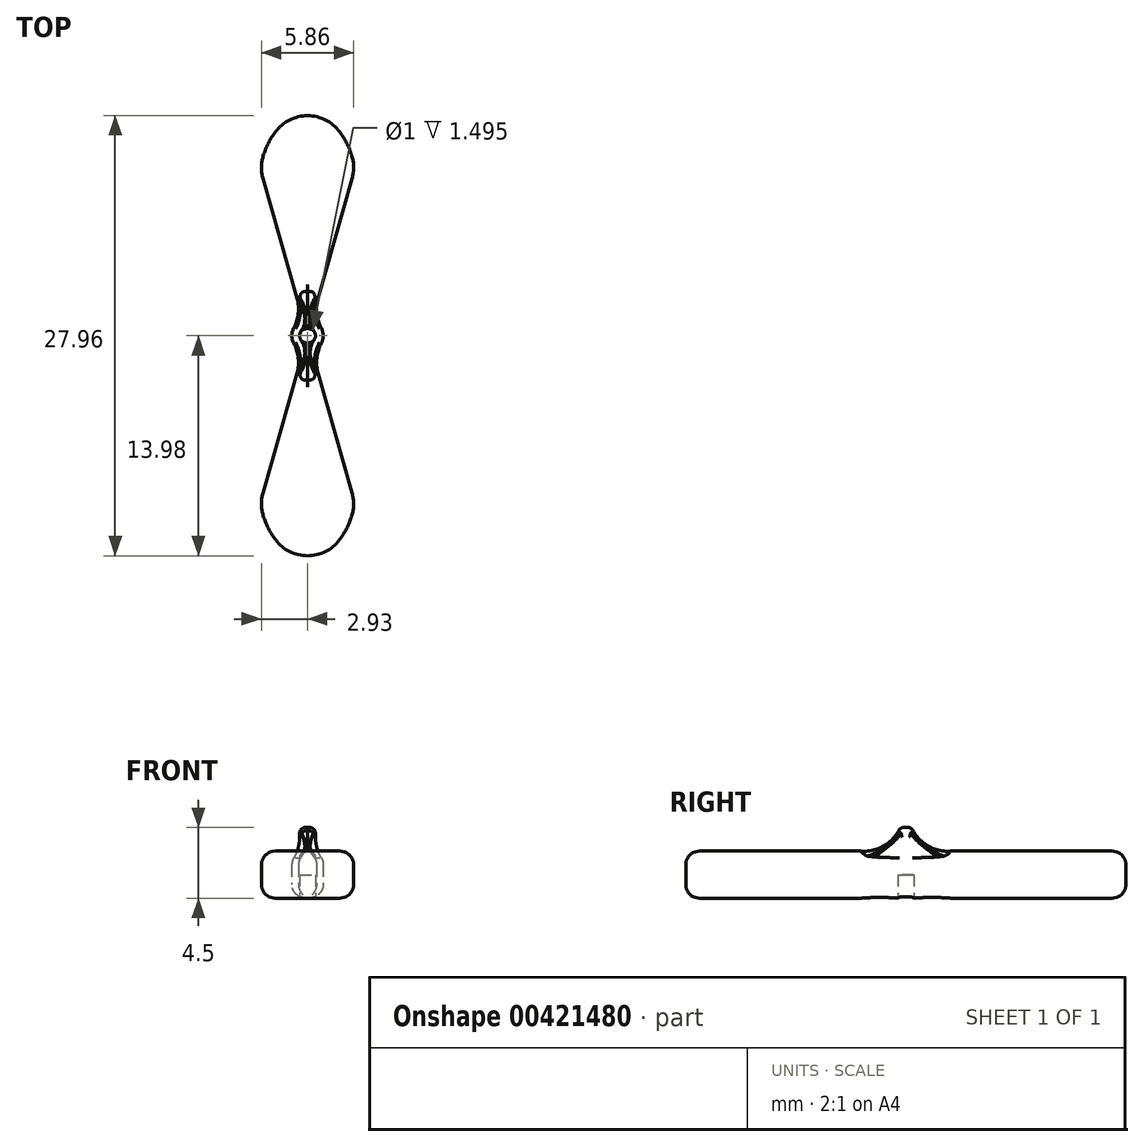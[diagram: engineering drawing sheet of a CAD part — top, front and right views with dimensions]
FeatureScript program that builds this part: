
annotation { "Feature Type Name" : "Feature", "Feature Type Description" : "" }
export const myFeature = defineFeature(function(context is Context, id is Id, definition is map)
    precondition{}
    {
        {
            var Q0;
            Q0=qCreatedBy(makeId("Top.planeOp"),FACE);
            var sketch = newSketch(context, id + "F0", { "sketchPlane" : qUnion([Q0])});
            skLineSegment(sketch, "E0", {"start": v(0, 0) * mm, "end": v(0, 15) * mm});
            skLineSegment(sketch, "E1", {"start": v(0, 15) * mm, "end": v(3, 15) * mm});
            skLineSegment(sketch, "E2", {"start": v(3, 15) * mm, "end": v(3, 10.58) * mm});
            skLineSegment(sketch, "E3", {"start": v(3, 10.58) * mm, "end": v(0, 0) * mm});
            skLineSegment(sketch, "E4.MirrorCS", {"start": v(0, 15) * mm, "end": v(-3, 15) * mm});
            skLineSegment(sketch, "E5.MirrorCS", {"start": v(-3, 15) * mm, "end": v(-3, 10.58) * mm});
            skLineSegment(sketch, "E6.MirrorCS", {"start": v(-3, 10.58) * mm, "end": v(0, 0) * mm});
            skLineSegment(sketch, "E7.MirrorCS", {"start": v(3, -10.58) * mm, "end": v(0, 0) * mm});
            skLineSegment(sketch, "E8.MirrorCS", {"start": v(-3, -10.58) * mm, "end": v(0, 0) * mm});
            skLineSegment(sketch, "E9.MirrorCS", {"start": v(3, -15) * mm, "end": v(3, -10.58) * mm});
            skLineSegment(sketch, "E10.MirrorCS", {"start": v(0, -15) * mm, "end": v(-3, -15) * mm});
            skLineSegment(sketch, "E11.MirrorCS", {"start": v(-3, -15) * mm, "end": v(-3, -10.58) * mm});
            skLineSegment(sketch, "E12.MirrorCS", {"start": v(0, -15) * mm, "end": v(3, -15) * mm});
            skLineSegment(sketch, "E13.MirrorCS", {"start": v(0, 0) * mm, "end": v(0, -15) * mm});
            skCircle(sketch, "E14", {"center": v(0, 0) * mm, "radius": 1 * mm});
            skSolve(sketch);
        }
        {
            var Q0;
            Q0 = qSketchRegion(id + "F0", true);
            extrude(context, id + "F1", {"entities" : qUnion([Q0]), "depth" : 3 * mm});
        }
        {
            var Q0;
            Q0=makeQuery(id+"F1.opExtrude","SWEPT_EDGE",EDGE,{"disambiguationData":[OSD([sQuery(id+"F0.wireOp",EDGE,"E9.MirrorCS"),sQuery(id+"F0.wireOp",EDGE,"E12.MirrorCS")])]});
            var Q1;
            Q1=makeQuery(id+"F1.opExtrude","SWEPT_EDGE",EDGE,{"disambiguationData":[OSD([sQuery(id+"F0.wireOp",EDGE,"E10.MirrorCS"),sQuery(id+"F0.wireOp",EDGE,"E11.MirrorCS")])]});
            var Q2;
            Q2=makeQuery(id+"F1.opExtrude","SWEPT_EDGE",EDGE,{"disambiguationData":[OSD([sQuery(id+"F0.wireOp",EDGE,"E1"),sQuery(id+"F0.wireOp",EDGE,"E2")])]});
            var Q3;
            Q3=makeQuery(id+"F1.opExtrude","SWEPT_EDGE",EDGE,{"disambiguationData":[OSD([sQuery(id+"F0.wireOp",EDGE,"E4.MirrorCS"),sQuery(id+"F0.wireOp",EDGE,"E5.MirrorCS")])]});
            fillet(context, id + "F2", {"entities" : qUnion([Q0, Q1, Q2, Q3]), "radius" : 5.08 * mm, "tangentPropagation" : true, "allowEdgeOverflow" : false});
        }
        {
            var Q0;
            Q0=makeQuery(id+"F2.opFillet","BLEND_EDGE",EDGE,{"blendedFrom":[makeQuery(id+"F1.opExtrude","SWEPT_EDGE",EDGE,{"disambiguationData":[OSD([sQuery(id+"F0.wireOp",EDGE,"E4.MirrorCS"),sQuery(id+"F0.wireOp",EDGE,"E5.MirrorCS")])]}),makeQuery(id+"F1.opExtrude","SWEPT_FACE",FACE,{"disambiguationData":[OSD([sQuery(id+"F0.wireOp",EDGE,"E6.MirrorCS")])]})],"blendedInto":[makeQuery(id+"F1.opExtrude","SWEPT_FACE",FACE,{"disambiguationData":[OSD([sQuery(id+"F0.wireOp",EDGE,"E6.MirrorCS")])]})]});
            var Q1;
            Q1=makeQuery(id+"F2.opFillet","BLEND_EDGE",EDGE,{"blendedFrom":[makeQuery(id+"F1.opExtrude","SWEPT_EDGE",EDGE,{"disambiguationData":[OSD([sQuery(id+"F0.wireOp",EDGE,"E1"),sQuery(id+"F0.wireOp",EDGE,"E2")])]}),makeQuery(id+"F1.opExtrude","SWEPT_FACE",FACE,{"disambiguationData":[OSD([sQuery(id+"F0.wireOp",EDGE,"E3")])]})],"blendedInto":[makeQuery(id+"F1.opExtrude","SWEPT_FACE",FACE,{"disambiguationData":[OSD([sQuery(id+"F0.wireOp",EDGE,"E3")])]})]});
            var Q2;
            Q2=makeQuery(id+"F2.opFillet","BLEND_EDGE",EDGE,{"blendedFrom":[makeQuery(id+"F1.opExtrude","SWEPT_EDGE",EDGE,{"disambiguationData":[OSD([sQuery(id+"F0.wireOp",EDGE,"E9.MirrorCS"),sQuery(id+"F0.wireOp",EDGE,"E12.MirrorCS")])]}),makeQuery(id+"F1.opExtrude","SWEPT_FACE",FACE,{"disambiguationData":[OSD([sQuery(id+"F0.wireOp",EDGE,"E7.MirrorCS")])]})],"blendedInto":[makeQuery(id+"F1.opExtrude","SWEPT_FACE",FACE,{"disambiguationData":[OSD([sQuery(id+"F0.wireOp",EDGE,"E7.MirrorCS")])]})]});
            var Q3;
            Q3=makeQuery(id+"F2.opFillet","BLEND_EDGE",EDGE,{"blendedFrom":[makeQuery(id+"F1.opExtrude","SWEPT_EDGE",EDGE,{"disambiguationData":[OSD([sQuery(id+"F0.wireOp",EDGE,"E10.MirrorCS"),sQuery(id+"F0.wireOp",EDGE,"E11.MirrorCS")])]}),makeQuery(id+"F1.opExtrude","SWEPT_FACE",FACE,{"disambiguationData":[OSD([sQuery(id+"F0.wireOp",EDGE,"E8.MirrorCS")])]})],"blendedInto":[makeQuery(id+"F1.opExtrude","SWEPT_FACE",FACE,{"disambiguationData":[OSD([sQuery(id+"F0.wireOp",EDGE,"E8.MirrorCS")])]})]});
            var Q4;
            Q4=makeQuery(id+"F2.opFillet","BLEND_EDGE",EDGE,{"blendedFrom":[makeQuery(id+"F1.opExtrude","SWEPT_EDGE",EDGE,{"disambiguationData":[OSD([sQuery(id+"F0.wireOp",EDGE,"E9.MirrorCS"),sQuery(id+"F0.wireOp",EDGE,"E12.MirrorCS")])]}),makeQuery(id+"F1.opExtrude","SWEPT_EDGE",EDGE,{"disambiguationData":[OSD([sQuery(id+"F0.wireOp",EDGE,"E10.MirrorCS"),sQuery(id+"F0.wireOp",EDGE,"E11.MirrorCS")])]})],"blendedInto":[]});
            var Q5;
            Q5=makeQuery(id+"F2.opFillet","BLEND_EDGE",EDGE,{"blendedFrom":[makeQuery(id+"F1.opExtrude","SWEPT_EDGE",EDGE,{"disambiguationData":[OSD([sQuery(id+"F0.wireOp",EDGE,"E1"),sQuery(id+"F0.wireOp",EDGE,"E2")])]}),makeQuery(id+"F1.opExtrude","SWEPT_EDGE",EDGE,{"disambiguationData":[OSD([sQuery(id+"F0.wireOp",EDGE,"E4.MirrorCS"),sQuery(id+"F0.wireOp",EDGE,"E5.MirrorCS")])]})],"blendedInto":[]});
            fillet(context, id + "F3", {"entities" : qUnion([Q0, Q1, Q2, Q3, Q4, Q5]), "radius" : 2.54 * mm, "tangentPropagation" : true, "allowEdgeOverflow" : false});
        }
        {
            var Q0;
            Q0 = qSketchRegion(id + "F0", true);
            extrude(context, id + "F4", {"entities" : qUnion([Q0]), "operationType" : NewBodyOperationType.ADD, "depth" : 3 * mm});
        }
        {
            var Q0;
            Q0=makeQuery(id+"F4.opExtrude","SWEPT_EDGE",EDGE,{"disambiguationData":[OSD([sQuery(id+"F0.wireOp",EDGE,"E4.MirrorCS"),sQuery(id+"F0.wireOp",EDGE,"E5.MirrorCS")])]});
            var Q1;
            Q1=makeQuery(id+"F4.opExtrude","SWEPT_EDGE",EDGE,{"disambiguationData":[OSD([sQuery(id+"F0.wireOp",EDGE,"E1"),sQuery(id+"F0.wireOp",EDGE,"E2")])]});
            var Q2;
            Q2=makeQuery(id+"F4.opExtrude","SWEPT_EDGE",EDGE,{"disambiguationData":[OSD([sQuery(id+"F0.wireOp",EDGE,"E10.MirrorCS"),sQuery(id+"F0.wireOp",EDGE,"E11.MirrorCS")])]});
            var Q3;
            Q3=makeQuery(id+"F4.opExtrude","SWEPT_EDGE",EDGE,{"disambiguationData":[OSD([sQuery(id+"F0.wireOp",EDGE,"E9.MirrorCS"),sQuery(id+"F0.wireOp",EDGE,"E12.MirrorCS")])]});
            fillet(context, id + "F5", {"entities" : qUnion([Q0, Q1, Q2, Q3]), "radius" : 5.08 * mm, "tangentPropagation" : true, "allowEdgeOverflow" : false});
        }
        {
            var Q0;
            {var subQ0=sQuery(id+"F0.wireOp",EDGE,"E6.MirrorCS");Q0=makeQuery(id+"F5.opFillet","BLEND_EDGE",EDGE,{"blendedFrom":[makeQuery(id+"F4.opExtrude","SWEPT_EDGE",EDGE,{"disambiguationData":[OSD([sQuery(id+"F0.wireOp",EDGE,"E4.MirrorCS"),sQuery(id+"F0.wireOp",EDGE,"E5.MirrorCS")])]}),makeQuery(id+"F4.boolean.opBoolean","MERGE",FACE,{"derivedFrom":[makeQuery(id+"F1.opExtrude","SWEPT_FACE",FACE,{"disambiguationData":[OSD([subQ0])]}),makeQuery(id+"F4.opExtrude","SWEPT_FACE",FACE,{"disambiguationData":[OSD([subQ0])]})]})],"blendedInto":[makeQuery(id+"F4.boolean.opBoolean","MERGE",FACE,{"derivedFrom":[makeQuery(id+"F1.opExtrude","SWEPT_FACE",FACE,{"disambiguationData":[OSD([subQ0])]}),makeQuery(id+"F4.opExtrude","SWEPT_FACE",FACE,{"disambiguationData":[OSD([subQ0])]})]})]});}
            var Q1;
            Q1=makeQuery(id+"F5.opFillet","BLEND_EDGE",EDGE,{"blendedFrom":[makeQuery(id+"F4.opExtrude","SWEPT_EDGE",EDGE,{"disambiguationData":[OSD([sQuery(id+"F0.wireOp",EDGE,"E1"),sQuery(id+"F0.wireOp",EDGE,"E2")])]}),makeQuery(id+"F4.opExtrude","SWEPT_EDGE",EDGE,{"disambiguationData":[OSD([sQuery(id+"F0.wireOp",EDGE,"E4.MirrorCS"),sQuery(id+"F0.wireOp",EDGE,"E5.MirrorCS")])]})],"blendedInto":[]});
            var Q2;
            {var subQ0=sQuery(id+"F0.wireOp",EDGE,"E3");Q2=makeQuery(id+"F5.opFillet","BLEND_EDGE",EDGE,{"blendedFrom":[makeQuery(id+"F4.opExtrude","SWEPT_EDGE",EDGE,{"disambiguationData":[OSD([sQuery(id+"F0.wireOp",EDGE,"E1"),sQuery(id+"F0.wireOp",EDGE,"E2")])]}),makeQuery(id+"F4.boolean.opBoolean","MERGE",FACE,{"derivedFrom":[makeQuery(id+"F1.opExtrude","SWEPT_FACE",FACE,{"disambiguationData":[OSD([subQ0])]}),makeQuery(id+"F4.opExtrude","SWEPT_FACE",FACE,{"disambiguationData":[OSD([subQ0])]})]})],"blendedInto":[makeQuery(id+"F4.boolean.opBoolean","MERGE",FACE,{"derivedFrom":[makeQuery(id+"F1.opExtrude","SWEPT_FACE",FACE,{"disambiguationData":[OSD([subQ0])]}),makeQuery(id+"F4.opExtrude","SWEPT_FACE",FACE,{"disambiguationData":[OSD([subQ0])]})]})]});}
            var Q3;
            {var subQ0=sQuery(id+"F0.wireOp",EDGE,"E7.MirrorCS");Q3=makeQuery(id+"F5.opFillet","BLEND_EDGE",EDGE,{"blendedFrom":[makeQuery(id+"F4.opExtrude","SWEPT_EDGE",EDGE,{"disambiguationData":[OSD([sQuery(id+"F0.wireOp",EDGE,"E9.MirrorCS"),sQuery(id+"F0.wireOp",EDGE,"E12.MirrorCS")])]}),makeQuery(id+"F4.boolean.opBoolean","MERGE",FACE,{"derivedFrom":[makeQuery(id+"F1.opExtrude","SWEPT_FACE",FACE,{"disambiguationData":[OSD([subQ0])]}),makeQuery(id+"F4.opExtrude","SWEPT_FACE",FACE,{"disambiguationData":[OSD([subQ0])]})]})],"blendedInto":[makeQuery(id+"F4.boolean.opBoolean","MERGE",FACE,{"derivedFrom":[makeQuery(id+"F1.opExtrude","SWEPT_FACE",FACE,{"disambiguationData":[OSD([subQ0])]}),makeQuery(id+"F4.opExtrude","SWEPT_FACE",FACE,{"disambiguationData":[OSD([subQ0])]})]})]});}
            var Q4;
            {var subQ0=sQuery(id+"F0.wireOp",EDGE,"E8.MirrorCS");Q4=makeQuery(id+"F5.opFillet","BLEND_EDGE",EDGE,{"blendedFrom":[makeQuery(id+"F4.opExtrude","SWEPT_EDGE",EDGE,{"disambiguationData":[OSD([sQuery(id+"F0.wireOp",EDGE,"E10.MirrorCS"),sQuery(id+"F0.wireOp",EDGE,"E11.MirrorCS")])]}),makeQuery(id+"F4.boolean.opBoolean","MERGE",FACE,{"derivedFrom":[makeQuery(id+"F1.opExtrude","SWEPT_FACE",FACE,{"disambiguationData":[OSD([subQ0])]}),makeQuery(id+"F4.opExtrude","SWEPT_FACE",FACE,{"disambiguationData":[OSD([subQ0])]})]})],"blendedInto":[makeQuery(id+"F4.boolean.opBoolean","MERGE",FACE,{"derivedFrom":[makeQuery(id+"F1.opExtrude","SWEPT_FACE",FACE,{"disambiguationData":[OSD([subQ0])]}),makeQuery(id+"F4.opExtrude","SWEPT_FACE",FACE,{"disambiguationData":[OSD([subQ0])]})]})]});}
            var Q5;
            Q5=makeQuery(id+"F1.opExtrude","SWEPT_EDGE",EDGE,{"disambiguationData":[OSD([sQuery(id+"F0.wireOp",EDGE,"E8.MirrorCS"),sQuery(id+"F0.wireOp",EDGE,"E14")])]});
            var Q6;
            Q6=makeQuery(id+"F1.opExtrude","SWEPT_EDGE",EDGE,{"disambiguationData":[OSD([sQuery(id+"F0.wireOp",EDGE,"E6.MirrorCS"),sQuery(id+"F0.wireOp",EDGE,"E14")])]});
            var Q7;
            Q7=makeQuery(id+"F1.opExtrude","SWEPT_EDGE",EDGE,{"disambiguationData":[OSD([sQuery(id+"F0.wireOp",EDGE,"E7.MirrorCS"),sQuery(id+"F0.wireOp",EDGE,"E14")])]});
            var Q8;
            Q8=makeQuery(id+"F1.opExtrude","SWEPT_EDGE",EDGE,{"disambiguationData":[OSD([sQuery(id+"F0.wireOp",EDGE,"E3"),sQuery(id+"F0.wireOp",EDGE,"E14")])]});
            var Q9;
            Q9=makeQuery(id+"F5.opFillet","BLEND_EDGE",EDGE,{"blendedFrom":[makeQuery(id+"F4.opExtrude","SWEPT_EDGE",EDGE,{"disambiguationData":[OSD([sQuery(id+"F0.wireOp",EDGE,"E9.MirrorCS"),sQuery(id+"F0.wireOp",EDGE,"E12.MirrorCS")])]}),makeQuery(id+"F4.opExtrude","SWEPT_EDGE",EDGE,{"disambiguationData":[OSD([sQuery(id+"F0.wireOp",EDGE,"E10.MirrorCS"),sQuery(id+"F0.wireOp",EDGE,"E11.MirrorCS")])]})],"blendedInto":[]});
            fillet(context, id + "F6", {"entities" : qUnion([Q0, Q1, Q2, Q3, Q4, Q5, Q6, Q7, Q8, Q9]), "radius" : 2.54 * mm, "tangentPropagation" : true, "allowEdgeOverflow" : false});
        }
        {
            var Q0;
            {var subQ0=sQuery(id+"F0.wireOp",EDGE,"E14");var subQ1=sQuery(id+"F0.wireOp",EDGE,"E12.MirrorCS");var subQ2=sQuery(id+"F0.wireOp",EDGE,"E11.MirrorCS");var subQ3=sQuery(id+"F0.wireOp",EDGE,"E10.MirrorCS");var subQ4=sQuery(id+"F0.wireOp",EDGE,"E9.MirrorCS");var subQ5=sQuery(id+"F0.wireOp",EDGE,"E8.MirrorCS");var subQ6=sQuery(id+"F0.wireOp",EDGE,"E7.MirrorCS");var subQ7=sQuery(id+"F0.wireOp",EDGE,"E6.MirrorCS");var subQ8=sQuery(id+"F0.wireOp",EDGE,"E5.MirrorCS");var subQ9=sQuery(id+"F0.wireOp",EDGE,"E4.MirrorCS");var subQ10=sQuery(id+"F0.wireOp",EDGE,"E3");var subQ11=sQuery(id+"F0.wireOp",EDGE,"E2");var subQ12=sQuery(id+"F0.wireOp",EDGE,"E1");Q0=makeQuery(id+"F4.boolean.opBoolean","MERGE",FACE,{"derivedFrom":[makeQuery(id+"F1.opExtrude","CAP_FACE",FACE,{"disambiguationData":[OSD([subQ12,subQ11,subQ10,subQ9,subQ8,subQ7,subQ6,subQ5,subQ4,subQ3,subQ2,subQ1,subQ0])],"isStart":true}),makeQuery(id+"F4.opExtrude","CAP_FACE",FACE,{"disambiguationData":[OSD([subQ12,subQ11,subQ10,subQ9,subQ8,subQ7,subQ6,subQ5,subQ4,subQ3,subQ2,subQ1,subQ0])],"isStart":true})]});}
            var sketch = newSketch(context, id + "F7", { "sketchPlane" : qUnion([Q0])});
            skCircle(sketch, "E15", {"center": v(0, 0) * mm, "radius": 0.5 * mm});
            skSolve(sketch);
        }
        {
            var Q0;
            Q0=makeQuery(id+"F7.imprint","IMPRINT",FACE,{"disambiguationData":[TD([[makeQuery(id+"F7.imprint","IMPRINT",EDGE,{"derivedFrom":sQuery(id+"F7.wireOp",EDGE,"E15")}),1.0]])]});
            extrude(context, id + "F8", {"entities" : qUnion([Q0]), "operationType" : NewBodyOperationType.REMOVE, "oppositeDirection" : true, "depth" : 1.5 * mm});
        }
        {
            var Q0;
            {var subQ0=sQuery(id+"F0.wireOp",EDGE,"E7.MirrorCS");Q0=makeQuery(id+"F4.boolean.opBoolean","MERGE",EDGE,{"derivedFrom":[makeQuery(id+"F1.opExtrude","CAP_EDGE",EDGE,{"disambiguationData":[OSD([subQ0])],"isStart":true}),makeQuery(id+"F4.opExtrude","CAP_EDGE",EDGE,{"disambiguationData":[OSD([subQ0])],"isStart":true})]});}
            var Q1;
            {var subQ0=sQuery(id+"F0.wireOp",EDGE,"E7.MirrorCS");Q1=makeQuery(id+"F4.boolean.opBoolean","MERGE",EDGE,{"derivedFrom":[makeQuery(id+"F1.opExtrude","CAP_EDGE",EDGE,{"disambiguationData":[OSD([subQ0])],"isStart":false}),makeQuery(id+"F4.opExtrude","CAP_EDGE",EDGE,{"disambiguationData":[OSD([subQ0])],"isStart":false})]});}
            fillet(context, id + "F9", {"entities" : qUnion([Q0, Q1]), "radius" : 0.89 * mm, "tangentPropagation" : true, "allowEdgeOverflow" : false});
        }
        {
            var Q0;
            Q0=makeQuery(id+"F8.boolean.opBoolean","COPY",FACE,{"derivedFrom":makeQuery(id+"F8.opExtrude","CAP_FACE",FACE,{"disambiguationData":[OSD([sQuery(id+"F7.wireOp",EDGE,"E15")])],"isStart":false})});
            extrude(context, id + "F10", {"entities" : qUnion([Q0]), "operationType" : NewBodyOperationType.ADD, "oppositeDirection" : true, "depth" : 3 * mm});
        }
        {
            var Q0;
            Q0=makeQuery(id+"F10.opExtrude","CAP_EDGE",EDGE,{"disambiguationData":[OSD([sQuery(id+"F7.wireOp",EDGE,"E15")])],"isStart":false});
            fillet(context, id + "F11", {"entities" : qUnion([Q0]), "radius" : 0.38 * mm, "tangentPropagation" : true, "allowEdgeOverflow" : false});
        }
        {
            var Q0;
            {var subQ0=sQuery(id+"F0.wireOp",EDGE,"E14");Q0=makeQuery(id+"F10.boolean.opBoolean","INTERSECT",EDGE,{"derivedFrom":[makeQuery(id+"F9.opFillet","BLEND_FACE",FACE,{"disambiguationData":[OSD([subQ0]),TDD([makeQuery(id+"F1.opExtrude","CAP_EDGE",EDGE,{"disambiguationData":[OSD([subQ0]),TDD([makeQuery(id+"F0.imprint","IMPRINT",EDGE,{"disambiguationData":[TD([[makeQuery(id+"F0.imprint","INTERSECT",VERTEX,{"derivedFrom":[sQuery(id+"F0.wireOp",EDGE,"E6.MirrorCS"),subQ0]}),-1.0]])],"derivedFrom":subQ0})])],"isStart":false})])]}),makeQuery(id+"F10.opExtrude","SWEPT_FACE",FACE,{"disambiguationData":[OSD([sQuery(id+"F7.wireOp",EDGE,"E15")])]})]});}
            var Q1;
            {var subQ0=sQuery(id+"F0.wireOp",EDGE,"E14");var subQ1=sQuery(id+"F0.wireOp",EDGE,"E12.MirrorCS");var subQ2=sQuery(id+"F0.wireOp",EDGE,"E11.MirrorCS");var subQ3=sQuery(id+"F0.wireOp",EDGE,"E10.MirrorCS");var subQ4=sQuery(id+"F0.wireOp",EDGE,"E9.MirrorCS");var subQ5=sQuery(id+"F0.wireOp",EDGE,"E8.MirrorCS");var subQ6=sQuery(id+"F0.wireOp",EDGE,"E7.MirrorCS");var subQ7=sQuery(id+"F0.wireOp",EDGE,"E6.MirrorCS");var subQ8=sQuery(id+"F0.wireOp",EDGE,"E5.MirrorCS");var subQ9=sQuery(id+"F0.wireOp",EDGE,"E4.MirrorCS");var subQ10=sQuery(id+"F0.wireOp",EDGE,"E3");var subQ11=sQuery(id+"F0.wireOp",EDGE,"E2");var subQ12=sQuery(id+"F0.wireOp",EDGE,"E1");Q1=makeQuery(id+"F10.boolean.opBoolean","INTERSECT",EDGE,{"derivedFrom":[makeQuery(id+"F9.opFillet","BLEND_FACE",FACE,{"disambiguationData":[OSD([subQ12,subQ11,subQ10,subQ9,subQ8,subQ7,subQ6,subQ5,subQ4,subQ3,subQ2,subQ1,subQ0]),TDD([makeQuery(id+"F6.opFillet","BLEND_EDGE",EDGE,{"blendedFrom":[makeQuery(id+"F1.opExtrude","SWEPT_EDGE",EDGE,{"disambiguationData":[OSD([subQ5,subQ0])]}),makeQuery(id+"F4.boolean.opBoolean","MERGE",FACE,{"derivedFrom":[makeQuery(id+"F1.opExtrude","CAP_FACE",FACE,{"disambiguationData":[OSD([subQ12,subQ11,subQ10,subQ9,subQ8,subQ7,subQ6,subQ5,subQ4,subQ3,subQ2,subQ1,subQ0])],"isStart":false}),makeQuery(id+"F4.opExtrude","CAP_FACE",FACE,{"disambiguationData":[OSD([subQ12,subQ11,subQ10,subQ9,subQ8,subQ7,subQ6,subQ5,subQ4,subQ3,subQ2,subQ1,subQ0])],"isStart":false})]})],"blendedInto":[makeQuery(id+"F4.boolean.opBoolean","MERGE",FACE,{"derivedFrom":[makeQuery(id+"F1.opExtrude","CAP_FACE",FACE,{"disambiguationData":[OSD([subQ12,subQ11,subQ10,subQ9,subQ8,subQ7,subQ6,subQ5,subQ4,subQ3,subQ2,subQ1,subQ0])],"isStart":false}),makeQuery(id+"F4.opExtrude","CAP_FACE",FACE,{"disambiguationData":[OSD([subQ12,subQ11,subQ10,subQ9,subQ8,subQ7,subQ6,subQ5,subQ4,subQ3,subQ2,subQ1,subQ0])],"isStart":false})]})]})])]}),makeQuery(id+"F10.opExtrude","SWEPT_FACE",FACE,{"disambiguationData":[OSD([sQuery(id+"F7.wireOp",EDGE,"E15")])]})]});}
            var Q2;
            {var subQ0=sQuery(id+"F0.wireOp",EDGE,"E14");var subQ1=sQuery(id+"F0.wireOp",EDGE,"E12.MirrorCS");var subQ2=sQuery(id+"F0.wireOp",EDGE,"E11.MirrorCS");var subQ3=sQuery(id+"F0.wireOp",EDGE,"E10.MirrorCS");var subQ4=sQuery(id+"F0.wireOp",EDGE,"E9.MirrorCS");var subQ5=sQuery(id+"F0.wireOp",EDGE,"E8.MirrorCS");var subQ6=sQuery(id+"F0.wireOp",EDGE,"E7.MirrorCS");var subQ7=sQuery(id+"F0.wireOp",EDGE,"E6.MirrorCS");var subQ8=sQuery(id+"F0.wireOp",EDGE,"E5.MirrorCS");var subQ9=sQuery(id+"F0.wireOp",EDGE,"E4.MirrorCS");var subQ10=sQuery(id+"F0.wireOp",EDGE,"E3");var subQ11=sQuery(id+"F0.wireOp",EDGE,"E2");var subQ12=sQuery(id+"F0.wireOp",EDGE,"E1");Q2=makeQuery(id+"F10.boolean.opBoolean","INTERSECT",EDGE,{"derivedFrom":[makeQuery(id+"F9.opFillet","BLEND_FACE",FACE,{"disambiguationData":[OSD([subQ12,subQ11,subQ10,subQ9,subQ8,subQ7,subQ6,subQ5,subQ4,subQ3,subQ2,subQ1,subQ0]),TDD([makeQuery(id+"F6.opFillet","BLEND_EDGE",EDGE,{"blendedFrom":[makeQuery(id+"F1.opExtrude","SWEPT_EDGE",EDGE,{"disambiguationData":[OSD([subQ7,subQ0])]}),makeQuery(id+"F4.boolean.opBoolean","MERGE",FACE,{"derivedFrom":[makeQuery(id+"F1.opExtrude","CAP_FACE",FACE,{"disambiguationData":[OSD([subQ12,subQ11,subQ10,subQ9,subQ8,subQ7,subQ6,subQ5,subQ4,subQ3,subQ2,subQ1,subQ0])],"isStart":false}),makeQuery(id+"F4.opExtrude","CAP_FACE",FACE,{"disambiguationData":[OSD([subQ12,subQ11,subQ10,subQ9,subQ8,subQ7,subQ6,subQ5,subQ4,subQ3,subQ2,subQ1,subQ0])],"isStart":false})]})],"blendedInto":[makeQuery(id+"F4.boolean.opBoolean","MERGE",FACE,{"derivedFrom":[makeQuery(id+"F1.opExtrude","CAP_FACE",FACE,{"disambiguationData":[OSD([subQ12,subQ11,subQ10,subQ9,subQ8,subQ7,subQ6,subQ5,subQ4,subQ3,subQ2,subQ1,subQ0])],"isStart":false}),makeQuery(id+"F4.opExtrude","CAP_FACE",FACE,{"disambiguationData":[OSD([subQ12,subQ11,subQ10,subQ9,subQ8,subQ7,subQ6,subQ5,subQ4,subQ3,subQ2,subQ1,subQ0])],"isStart":false})]})]})])]}),makeQuery(id+"F10.opExtrude","SWEPT_FACE",FACE,{"disambiguationData":[OSD([sQuery(id+"F7.wireOp",EDGE,"E15")])]})]});}
            var Q3;
            {var subQ0=sQuery(id+"F0.wireOp",EDGE,"E14");var subQ1=sQuery(id+"F0.wireOp",EDGE,"E12.MirrorCS");var subQ2=sQuery(id+"F0.wireOp",EDGE,"E11.MirrorCS");var subQ3=sQuery(id+"F0.wireOp",EDGE,"E10.MirrorCS");var subQ4=sQuery(id+"F0.wireOp",EDGE,"E9.MirrorCS");var subQ5=sQuery(id+"F0.wireOp",EDGE,"E8.MirrorCS");var subQ6=sQuery(id+"F0.wireOp",EDGE,"E7.MirrorCS");var subQ7=sQuery(id+"F0.wireOp",EDGE,"E6.MirrorCS");var subQ8=sQuery(id+"F0.wireOp",EDGE,"E5.MirrorCS");var subQ9=sQuery(id+"F0.wireOp",EDGE,"E4.MirrorCS");var subQ10=sQuery(id+"F0.wireOp",EDGE,"E3");var subQ11=sQuery(id+"F0.wireOp",EDGE,"E2");var subQ12=sQuery(id+"F0.wireOp",EDGE,"E1");Q3=makeQuery(id+"F10.boolean.opBoolean","INTERSECT",EDGE,{"derivedFrom":[makeQuery(id+"F9.opFillet","BLEND_FACE",FACE,{"disambiguationData":[OSD([subQ12,subQ11,subQ10,subQ9,subQ8,subQ7,subQ6,subQ5,subQ4,subQ3,subQ2,subQ1,subQ0]),TDD([makeQuery(id+"F6.opFillet","BLEND_EDGE",EDGE,{"blendedFrom":[makeQuery(id+"F1.opExtrude","SWEPT_EDGE",EDGE,{"disambiguationData":[OSD([subQ10,subQ0])]}),makeQuery(id+"F4.boolean.opBoolean","MERGE",FACE,{"derivedFrom":[makeQuery(id+"F1.opExtrude","CAP_FACE",FACE,{"disambiguationData":[OSD([subQ12,subQ11,subQ10,subQ9,subQ8,subQ7,subQ6,subQ5,subQ4,subQ3,subQ2,subQ1,subQ0])],"isStart":false}),makeQuery(id+"F4.opExtrude","CAP_FACE",FACE,{"disambiguationData":[OSD([subQ12,subQ11,subQ10,subQ9,subQ8,subQ7,subQ6,subQ5,subQ4,subQ3,subQ2,subQ1,subQ0])],"isStart":false})]})],"blendedInto":[makeQuery(id+"F4.boolean.opBoolean","MERGE",FACE,{"derivedFrom":[makeQuery(id+"F1.opExtrude","CAP_FACE",FACE,{"disambiguationData":[OSD([subQ12,subQ11,subQ10,subQ9,subQ8,subQ7,subQ6,subQ5,subQ4,subQ3,subQ2,subQ1,subQ0])],"isStart":false}),makeQuery(id+"F4.opExtrude","CAP_FACE",FACE,{"disambiguationData":[OSD([subQ12,subQ11,subQ10,subQ9,subQ8,subQ7,subQ6,subQ5,subQ4,subQ3,subQ2,subQ1,subQ0])],"isStart":false})]})]})])]}),makeQuery(id+"F10.opExtrude","SWEPT_FACE",FACE,{"disambiguationData":[OSD([sQuery(id+"F7.wireOp",EDGE,"E15")])]})]});}
            var Q4;
            {var subQ0=sQuery(id+"F0.wireOp",EDGE,"E14");Q4=makeQuery(id+"F10.boolean.opBoolean","INTERSECT",EDGE,{"derivedFrom":[makeQuery(id+"F9.opFillet","BLEND_FACE",FACE,{"disambiguationData":[OSD([subQ0]),TDD([makeQuery(id+"F1.opExtrude","CAP_EDGE",EDGE,{"disambiguationData":[OSD([subQ0]),TDD([makeQuery(id+"F0.imprint","IMPRINT",EDGE,{"disambiguationData":[TD([[makeQuery(id+"F0.imprint","INTERSECT",VERTEX,{"derivedFrom":[sQuery(id+"F0.wireOp",EDGE,"E3"),subQ0]}),1.0]])],"derivedFrom":subQ0})])],"isStart":false})])]}),makeQuery(id+"F10.opExtrude","SWEPT_FACE",FACE,{"disambiguationData":[OSD([sQuery(id+"F7.wireOp",EDGE,"E15")])]})]});}
            var Q5;
            {var subQ0=sQuery(id+"F0.wireOp",EDGE,"E14");var subQ1=sQuery(id+"F0.wireOp",EDGE,"E12.MirrorCS");var subQ2=sQuery(id+"F0.wireOp",EDGE,"E11.MirrorCS");var subQ3=sQuery(id+"F0.wireOp",EDGE,"E10.MirrorCS");var subQ4=sQuery(id+"F0.wireOp",EDGE,"E9.MirrorCS");var subQ5=sQuery(id+"F0.wireOp",EDGE,"E8.MirrorCS");var subQ6=sQuery(id+"F0.wireOp",EDGE,"E7.MirrorCS");var subQ7=sQuery(id+"F0.wireOp",EDGE,"E6.MirrorCS");var subQ8=sQuery(id+"F0.wireOp",EDGE,"E5.MirrorCS");var subQ9=sQuery(id+"F0.wireOp",EDGE,"E4.MirrorCS");var subQ10=sQuery(id+"F0.wireOp",EDGE,"E3");var subQ11=sQuery(id+"F0.wireOp",EDGE,"E2");var subQ12=sQuery(id+"F0.wireOp",EDGE,"E1");Q5=makeQuery(id+"F10.boolean.opBoolean","INTERSECT",EDGE,{"derivedFrom":[makeQuery(id+"F9.opFillet","BLEND_FACE",FACE,{"disambiguationData":[OSD([subQ12,subQ11,subQ10,subQ9,subQ8,subQ7,subQ6,subQ5,subQ4,subQ3,subQ2,subQ1,subQ0]),TDD([makeQuery(id+"F6.opFillet","BLEND_EDGE",EDGE,{"blendedFrom":[makeQuery(id+"F1.opExtrude","SWEPT_EDGE",EDGE,{"disambiguationData":[OSD([subQ6,subQ0])]}),makeQuery(id+"F4.boolean.opBoolean","MERGE",FACE,{"derivedFrom":[makeQuery(id+"F1.opExtrude","CAP_FACE",FACE,{"disambiguationData":[OSD([subQ12,subQ11,subQ10,subQ9,subQ8,subQ7,subQ6,subQ5,subQ4,subQ3,subQ2,subQ1,subQ0])],"isStart":false}),makeQuery(id+"F4.opExtrude","CAP_FACE",FACE,{"disambiguationData":[OSD([subQ12,subQ11,subQ10,subQ9,subQ8,subQ7,subQ6,subQ5,subQ4,subQ3,subQ2,subQ1,subQ0])],"isStart":false})]})],"blendedInto":[makeQuery(id+"F4.boolean.opBoolean","MERGE",FACE,{"derivedFrom":[makeQuery(id+"F1.opExtrude","CAP_FACE",FACE,{"disambiguationData":[OSD([subQ12,subQ11,subQ10,subQ9,subQ8,subQ7,subQ6,subQ5,subQ4,subQ3,subQ2,subQ1,subQ0])],"isStart":false}),makeQuery(id+"F4.opExtrude","CAP_FACE",FACE,{"disambiguationData":[OSD([subQ12,subQ11,subQ10,subQ9,subQ8,subQ7,subQ6,subQ5,subQ4,subQ3,subQ2,subQ1,subQ0])],"isStart":false})]})]})])]}),makeQuery(id+"F10.opExtrude","SWEPT_FACE",FACE,{"disambiguationData":[OSD([sQuery(id+"F7.wireOp",EDGE,"E15")])]})]});}
            fillet(context, id + "F12", {"entities" : qUnion([Q0, Q1, Q2, Q3, Q4, Q5]), "radius" : 2.54 * mm, "tangentPropagation" : true, "allowEdgeOverflow" : false});
        }
    });
